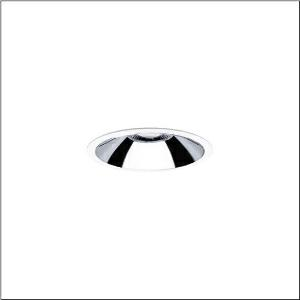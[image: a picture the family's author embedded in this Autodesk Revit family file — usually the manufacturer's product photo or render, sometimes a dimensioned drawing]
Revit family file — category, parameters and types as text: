
# Revit family: lunis_21_l_51db15md4c
name_source: partatom
category: Lighting Fixtures
units: mm (PartAtom-declared; Revit-internal decimal feet)

## family parameters
Cut with Voids When Loaded = No
Host = Face
Light Source = No
Part Type = Normal
Room Calculation Point = No
Round Connector Dimension = Use Diameter
Shared = No

## types (1)
- --- (1 x LED, 1700 lm, 13.8 W, 4000K)
    Apparent Load = 14 VA
    CIE Flux Codes = 90 99 100 100 100
    Color Rendering = 80
    Color Temperature = 4000K
    Default Elevation = 1800 mm
    Description = Lunis 21,  L, downlight, of PC, light emission: direct distribution, LED rated luminous flux: 1.700lm, light colour: 840, control gear: ECG, with terminal, 3-pole, mains connection: 220..240V, AC, housing, round, of diecast aluminium, traffic white (RAL 9016), diameter: 162mm, protection rating (complete): IP20, protection rating (on room side): IP54, insulation class (complete): insulation class II (safety insulation), certification: CE, impact resistance: IK02, packaging unit: 1 piece
    Height = 0 mm  [stored 0 ft]
    Lamp = 1 x LED
    Lamp Light Flux = 1700 lm
    Lamp Power = 13.8 W
    Lamp count = 1
    Length = 162 mm
    Luminous efficacy = 123 lm/W
    Manufacturer = Siteco
    ModVariant = No
    Model = 51DB15MD4C
    Mounting Place = Ceiling
    Mounting Type = Recessed
    Number of Poles = 1
    OnlyDefault = Yes
    Power Factor = 1
    Product Name = Lunis 21 L
    Product group = downlight
    ProductGroupID = 400
    Protection Class = Protection class II
    Protection Degree = IP 20
    RLX_Detail_Level = 1
    RLX_Emergency_Light_Flux = 0 lm
    RLX_Emergency_Type = 0
    RLX_Emergency_Type_DB = No
    RlxData = <blob elided: 21925 chars, md5=960c8fc4>
    Socket = socket
    Standby Power = 0 W
    System Light Flux = 1700 lm
    System Power = 14 W
    Type Comments = factory setting: luminous flux: 100 % | (ON | ON)
    Type Image = l_1287387.jpg
    URL = http://relux.com
    VarID = @adj_099569
    Voltage = 0 V
    Weight = 0.00 kg
    Width = 0 mm  [stored 0 ft]

note: [stored X ft] marks values corroborated as IEEE doubles in the binary element streams (Revit-internal decimal feet)

## geometry (parser evidence)
native form markers: Blend x4, Sweep x10
no freeform markers — native parametric forms only
